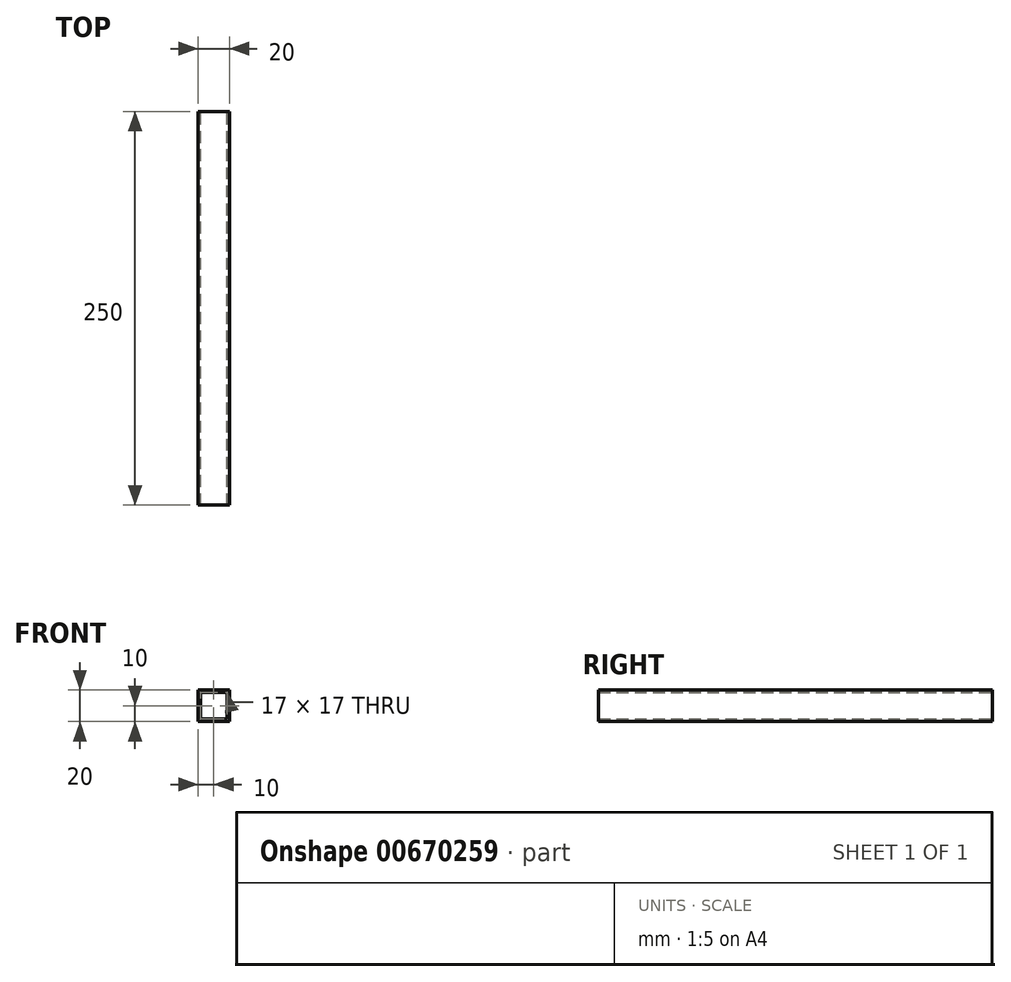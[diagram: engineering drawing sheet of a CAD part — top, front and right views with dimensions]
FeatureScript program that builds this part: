
annotation { "Feature Type Name" : "Feature", "Feature Type Description" : "" }
export const myFeature = defineFeature(function(context is Context, id is Id, definition is map)
    precondition{}
    {
        {
            var Q0;
            Q0=qCreatedBy(makeId("Front.planeOp"),FACE);
            var sketch = newSketch(context, id + "F0", { "sketchPlane" : qUnion([Q0])});
            skLineSegment(sketch, "E0.bottom", {"start": v(-10, 10) * mm, "end": v(10, 10) * mm});
            skLineSegment(sketch, "E0.top", {"start": v(-10, -10) * mm, "end": v(10, -10) * mm});
            skLineSegment(sketch, "E0.left", {"start": v(-10, 10) * mm, "end": v(-10, -10) * mm});
            skLineSegment(sketch, "E0.right", {"start": v(10, 10) * mm, "end": v(10, -10) * mm});
            skLineSegment(sketch, "E1.bottom", {"start": v(-8.5, 8.5) * mm, "end": v(8.5, 8.5) * mm});
            skLineSegment(sketch, "E1.top", {"start": v(-8.5, -8.5) * mm, "end": v(8.5, -8.5) * mm});
            skLineSegment(sketch, "E1.left", {"start": v(-8.5, 8.5) * mm, "end": v(-8.5, -8.5) * mm});
            skLineSegment(sketch, "E1.right", {"start": v(8.5, 8.5) * mm, "end": v(8.5, -8.5) * mm});
            skSolve(sketch);
        }
        {
            var Q0;
            Q0=qSketchRegion(id+"F0",true);
            extrude(context, id + "F1", {"entities" : qUnion([Q0]), "depth" : 250 * mm, "offsetDistance" : 25 * mm});
        }
    });
